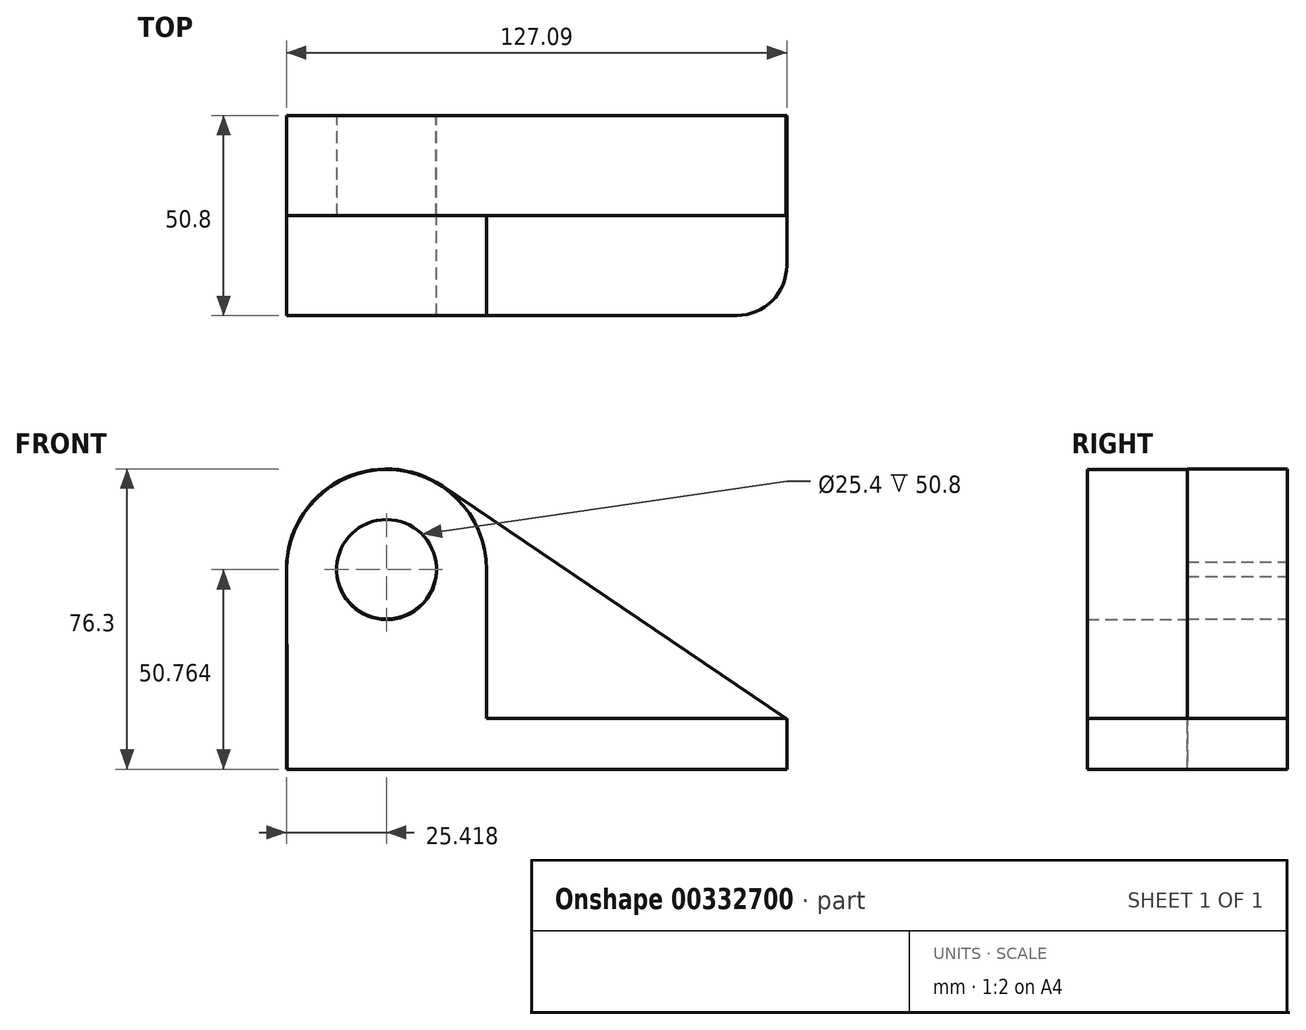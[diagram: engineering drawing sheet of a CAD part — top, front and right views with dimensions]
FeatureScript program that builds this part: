
annotation { "Feature Type Name" : "Feature", "Feature Type Description" : "" }
export const myFeature = defineFeature(function(context is Context, id is Id, definition is map)
    precondition{}
    {
        {
            var Q0;
            Q0=qCreatedBy(makeId("Front.planeOp"),FACE);
            var sketch = newSketch(context, id + "F0", { "sketchPlane" : qUnion([Q0])});
            skArc(sketch, "E0", {"start": v(-27.04, 54.37) * mm, "mid": v(-53.19, 55.77) * mm, "end": v(-66.68, 33.33) * mm});
            skLineSegment(sketch, "E1", {"start": v(-66.68, 33.33) * mm, "end": v(-66.68, -17.47) * mm});
            skLineSegment(sketch, "E2", {"start": v(-66.68, -17.47) * mm, "end": v(60.32, -17.47) * mm});
            skLineSegment(sketch, "E3", {"start": v(60.32, -17.47) * mm, "end": v(60.32, -4.77) * mm});
            skLineSegment(sketch, "E4", {"start": v(60.32, -4.77) * mm, "end": v(-27.04, 54.37) * mm});
            skCircle(sketch, "E5", {"center": v(-41.28, 33.33) * mm, "radius": 12.7 * mm});
            skSolve(sketch);
        }
        {
            var Q0;
            Q0=makeQuery(id+"F0.imprint","IMPRINT",FACE,{"disambiguationData":[TD([[makeQuery(id+"F0.imprint","IMPRINT",EDGE,{"derivedFrom":sQuery(id+"F0.wireOp",EDGE,"E0")}),1.0]])]});
            extrude(context, id + "F1", {"entities" : qUnion([Q0]), "depth" : 25.4 * mm});
        }
        {
            var Q0;
            Q0=qCreatedBy(makeId("Front.planeOp"),FACE);
            var sketch = newSketch(context, id + "F2", { "sketchPlane" : qUnion([Q0])});
            skCircle(sketch, "E6", {"center": v(-41.26, 33.2) * mm, "radius": 12.7 * mm});
            skArc(sketch, "E7", {"start": v(-15.86, 33.2) * mm, "mid": v(-41.31, 58.6) * mm, "end": v(-66.66, 33.1) * mm});
            skLineSegment(sketch, "E8.bottom", {"start": v(60.4, -4.67) * mm, "end": v(-15.86, -4.67) * mm});
            skLineSegment(sketch, "E8.top", {"start": v(60.4, -17.57) * mm, "end": v(-66.59, -17.57) * mm});
            skLineSegment(sketch, "E8.left", {"start": v(60.4, -4.67) * mm, "end": v(60.4, -17.57) * mm});
            skLineSegment(sketch, "E8.right", {"start": v(-66.59, -4.67) * mm, "end": v(-66.59, -17.57) * mm});
            skLineSegment(sketch, "E9", {"start": v(-15.86, 33.2) * mm, "end": v(-15.86, -4.67) * mm});
            skLineSegment(sketch, "E10", {"start": v(-66.66, 33.2) * mm, "end": v(-66.59, -4.67) * mm});
            skSolve(sketch);
        }
        {
            var Q0;
            Q0=makeQuery(id+"F2.imprint","IMPRINT",FACE,{"disambiguationData":[TD([[makeQuery(id+"F2.imprint","IMPRINT",EDGE,{"derivedFrom":sQuery(id+"F2.wireOp",EDGE,"E6")}),-1.0]])]});
            extrude(context, id + "F3", {"entities" : qUnion([Q0]), "operationType" : NewBodyOperationType.ADD, "depth" : 50.8 * mm});
        }
        {
            var Q0;
            Q0=makeQuery(id+"F3.opExtrude","CAP_EDGE",EDGE,{"disambiguationData":[OSD([sQuery(id+"F2.wireOp",EDGE,"E8.left")])],"isStart":false});
            fillet(context, id + "F4", {"entities" : qUnion([Q0]), "radius" : 12.7 * mm, "tangentPropagation" : true, "allowEdgeOverflow" : false});
        }
    });
